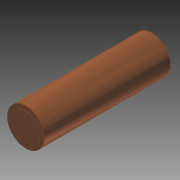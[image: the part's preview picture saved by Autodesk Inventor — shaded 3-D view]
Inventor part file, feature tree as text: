
AUTODESK INVENTOR PART (.ipt)
format: ipt  version: 2012 (Build 160160000, 160)  size: 87,552 bytes
history: native  units: mm
features: extrude x3, sketch x3
ambient origin geometry x8: Origin, YZ Plane, XZ Plane, XY Plane, X Axis, Y Axis, Z Axis, Center Point
bodies: Solid1 (feature_tree)
feature tree (6):
  extrude  "Extrusion1"  Depth=5.5mm
  extrude  "Extrusion2"  Depth=11.0mm
  extrude  "Extrusion3"  [1 undecoded]
  sketch  "Sketch1"  dims[d1=49.4mm d2=0.0mm d3=5.5mm]
  sketch  "Sketch2"  dims[d4=1.0mm d5=0.0mm d6=11.0mm]
  sketch  "Sketch3"  dims[d7=0.1mm d8=0.0mm]
note: 1 required parameter value undecoded (feature->parameter linkage not recoverable at this tier; creation-order binding heuristic only, values carry confidence <= 0.55)
